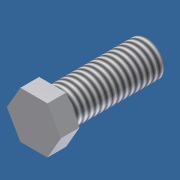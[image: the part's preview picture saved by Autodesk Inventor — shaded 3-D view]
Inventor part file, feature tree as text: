
AUTODESK INVENTOR PART (.ipt)
format: ipt  version: 2011 (Build 150239000, 239)  size: 88,064 bytes
history: native  units: in
note: dims shown in document units (in); Inventor stores cm internally (conversion verified against a paired STEP export)
features: extrude x2, sketch x1, thread x1
ambient origin geometry x8: Origin, YZ Plane, XZ Plane, XY Plane, X Axis, Y Axis, Z Axis, Center Point
bodies: Solid1 (feature_tree)
feature tree (4):
  sketch  "Sketch1"  dims[d10=0.5in d11=1.0in d12=0.0in d13=0.2in d14=0.0in d20=0.375in d21=1.0in d22=0.0in]
  extrude  "Extrusion1"  Depth=1.0in TaperAngle=0.0deg
  extrude  "Extrusion2"  Depth=0.2in TaperAngle=0.0deg
  thread  "Thread2"  [1 undecoded]
note: 1 required parameter value undecoded (feature->parameter linkage not recoverable at this tier; creation-order binding heuristic only, values carry confidence <= 0.55)
